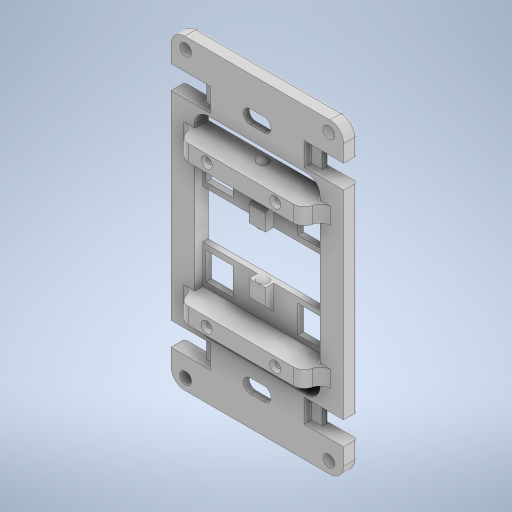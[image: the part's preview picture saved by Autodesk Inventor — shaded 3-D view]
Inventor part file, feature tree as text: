
AUTODESK INVENTOR PART (.ipt)
format: ipt  version: 2023 (Build 270158000, 158)  size: 620,032 bytes
history: native  units: mm
features: extrude x12, sketch x12, fillet x6, other x3, mirror x3, chamfer x2, revolve x1, projected_geometry x1
ambient origin geometry x8: Origin, YZ Plane, XZ Plane, XY Plane, X Axis, Y Axis, Z Axis, Center Point
bodies: Body1 (feature_tree)
feature tree (40):
  other  "솔리드1"
  extrude  "돌출1"  Depth=63.1mm
  extrude  "돌출2"  Depth=112.2mm
  extrude  "돌출3"  Depth=45.85mm
  fillet  "모깎기1"  Radius=70.23mm
  sketch  "스케치4"
  extrude  "돌출4"  Depth=5.0mm TaperAngle=0.0deg
  extrude  "돌출5"  Depth=5.0mm
  mirror  "미러1"
  mirror  "미러2"
  extrude  "돌출6"  Depth=5.0mm
  fillet  "모깎기2"  Radius=5.0mm
  mirror  "미러3"
  fillet  "모깎기3"  Radius=10.0mm
  other  "작업 평면1"
  sketch  "스케치9"
  extrude  "돌출8"  Depth=104.0mm
  extrude  "돌출9"  Depth=4.2mm
  fillet  "모깎기7"  Radius=52.4mm
  chamfer  "모따기1"  [1 undecoded]
  other  "작업 평면2"
  extrude  "돌출10"  Depth=5.0mm
  fillet  "모깎기9"  Radius=7.0mm
  fillet  "모깎기10"  Radius=8.5mm
  extrude  "돌출11"  Depth=3.4mm
  extrude  "돌출12"  Depth=11.2mm
  chamfer  "모따기2"  Distance=4.0mm
  revolve  "회전3"
  sketch  "스케치18"
  extrude  "돌출13"  TaperAngle=0.0deg  [1 undecoded]
  sketch  "스케치1"
  sketch  "스케치2"
  sketch  "스케치3"
  sketch  "스케치6"
  projected_geometry  "투영된 루프1"
  sketch  "스케치13"
  sketch  "스케치15"
  sketch  "스케치16"
  sketch  "스케치17"
  sketch  "스케치19"
note: 2 required parameter values undecoded (feature->parameter linkage not recoverable at this tier; creation-order binding heuristic only, values carry confidence <= 0.55)
